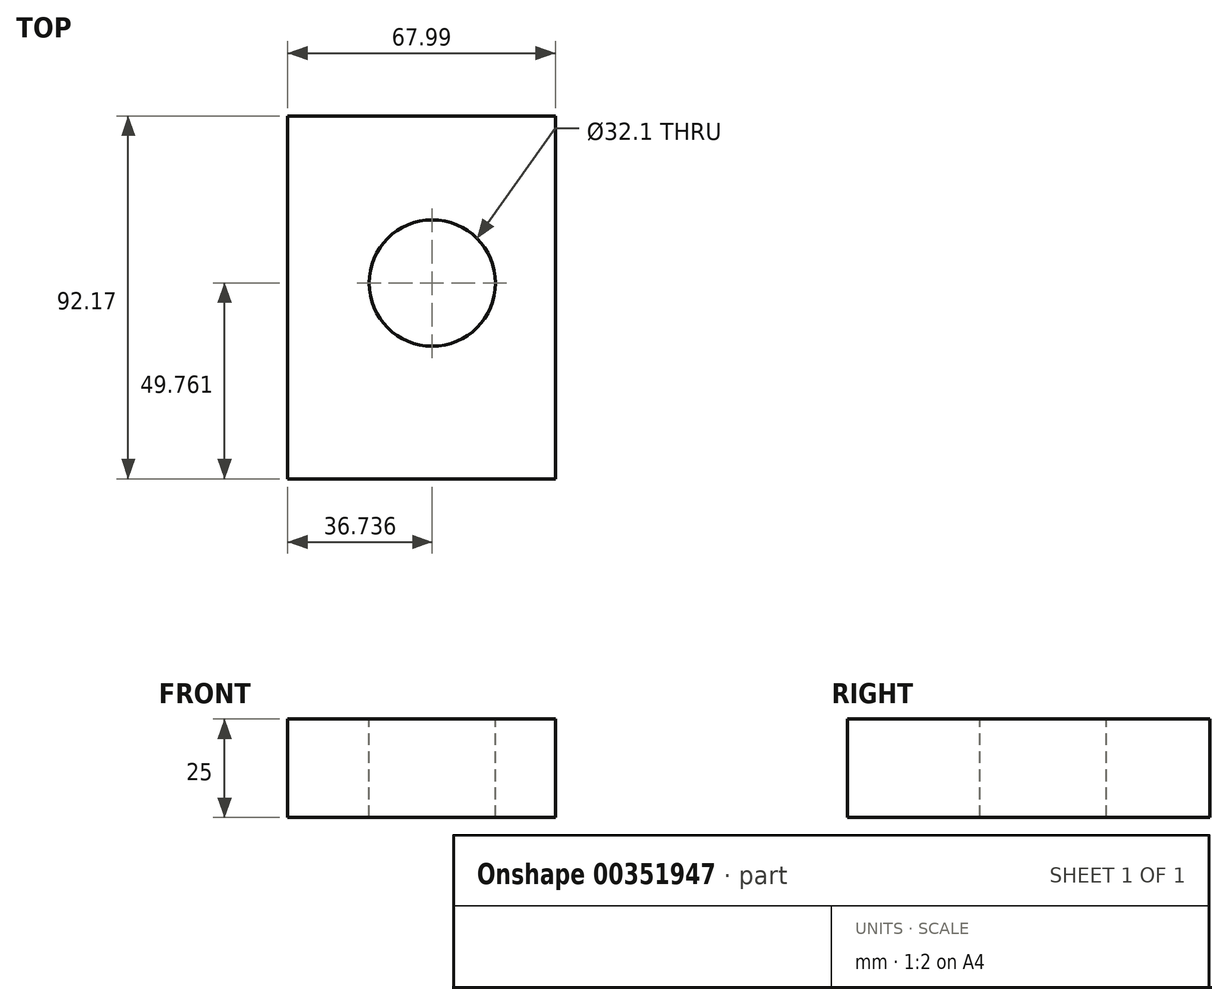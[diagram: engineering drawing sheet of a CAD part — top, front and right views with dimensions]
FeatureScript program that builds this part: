
annotation { "Feature Type Name" : "Feature", "Feature Type Description" : "" }
export const myFeature = defineFeature(function(context is Context, id is Id, definition is map)
    precondition{}
    {
        {
            var Q0;
            Q0=qCreatedBy(makeId("Top.planeOp"),FACE);
            var sketch = newSketch(context, id + "F0", { "sketchPlane" : qUnion([Q0])});
            skLineSegment(sketch, "E0.bottom", {"start": v(0, 0) * mm, "end": v(68, 0) * mm});
            skLineSegment(sketch, "E0.top", {"start": v(0, 92.17) * mm, "end": v(68, 92.17) * mm});
            skLineSegment(sketch, "E0.left", {"start": v(0, 0) * mm, "end": v(0, 92.17) * mm});
            skLineSegment(sketch, "E0.right", {"start": v(68, 0) * mm, "end": v(68, 92.17) * mm});
            skSolve(sketch);
        }
        {
            var Q0;
            Q0=makeQuery(id+"F0.imprint","IMPRINT",FACE,{"disambiguationData":[TD([[makeQuery(id+"F0.imprint","IMPRINT",EDGE,{"derivedFrom":sQuery(id+"F0.wireOp",EDGE,"E0.bottom")}),1.0]])]});
            var Q1;
            Q1=sQuery(id+"F0.wireOp",EDGE,"E0.top");
            extrude(context, id + "F1", {"entities" : qUnion([Q0]), "surfaceEntities" : qUnion([Q1]), "depth" : 25 * mm});
        }
        {
            var Q0;
            Q0=makeQuery(id+"F1.opExtrude","CAP_FACE",FACE,{"disambiguationData":[OSD([sQuery(id+"F0.wireOp",EDGE,"E0.bottom"),sQuery(id+"F0.wireOp",EDGE,"E0.top"),sQuery(id+"F0.wireOp",EDGE,"E0.left"),sQuery(id+"F0.wireOp",EDGE,"E0.right")])],"isStart":false});
            var sketch = newSketch(context, id + "F2", { "sketchPlane" : qUnion([Q0])});
            skCircle(sketch, "E1", {"center": v(36.74, 49.76) * mm, "radius": 16.05 * mm});
            skSolve(sketch);
        }
        {
            var Q0;
            Q0 = qSketchRegion(id + "F2", true);
            extrude(context, id + "F3", {"entities" : qUnion([Q0]), "operationType" : NewBodyOperationType.REMOVE, "oppositeDirection" : true, "depth" : 25 * mm});
        }
    });
